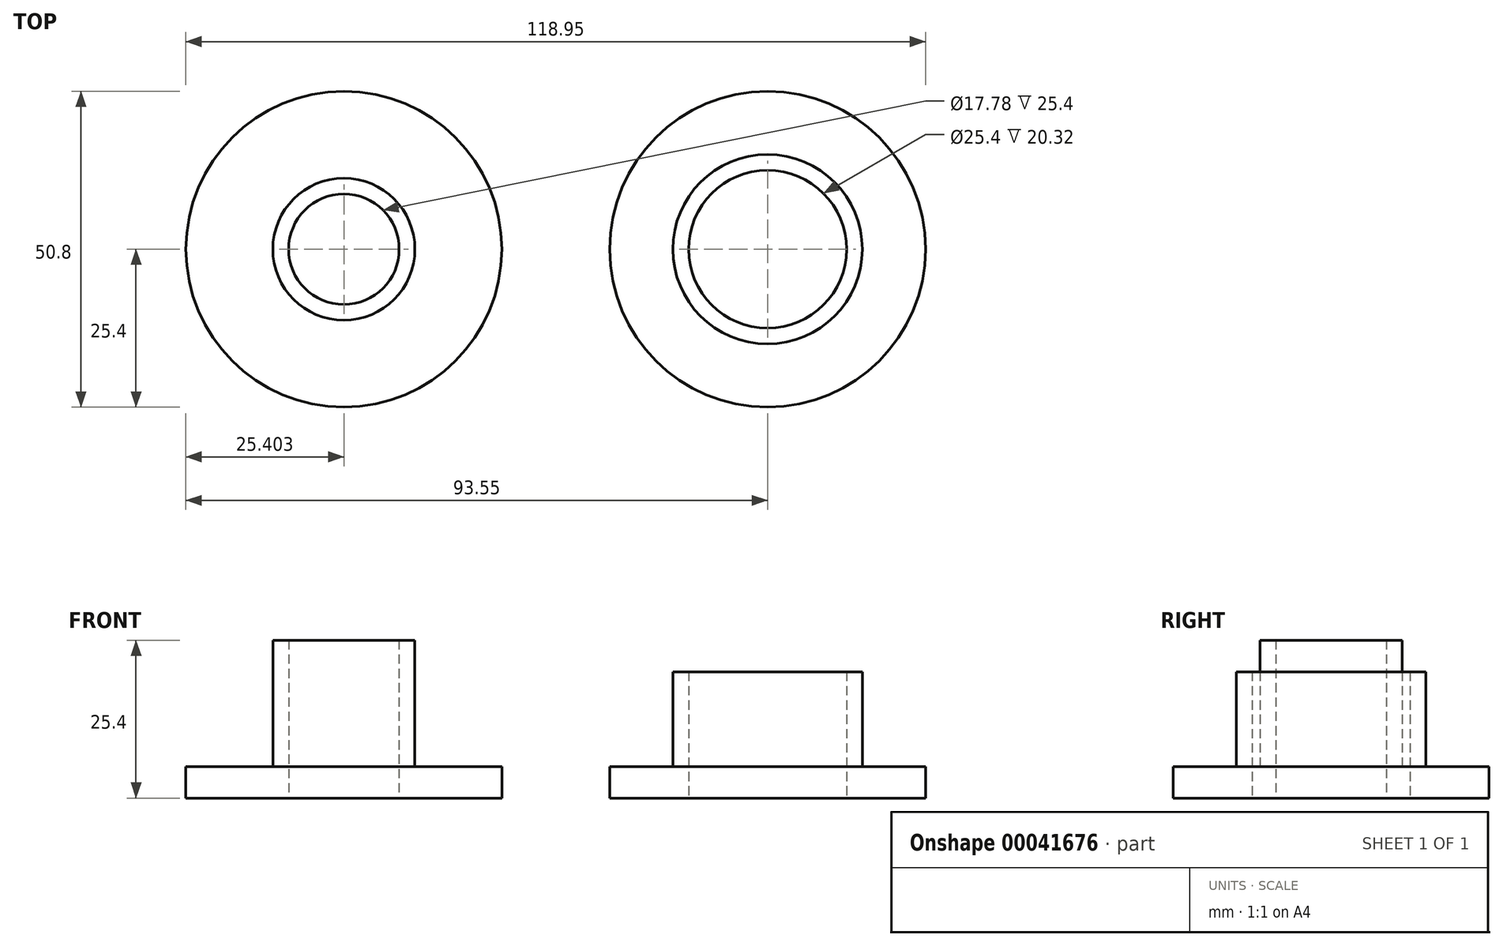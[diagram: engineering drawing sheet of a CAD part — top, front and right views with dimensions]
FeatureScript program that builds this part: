
annotation { "Feature Type Name" : "Feature", "Feature Type Description" : "" }
export const myFeature = defineFeature(function(context is Context, id is Id, definition is map)
    precondition{}
    {
        {
            var Q0;
            Q0=qCreatedBy(makeId("Top.planeOp"),FACE);
            var sketch = newSketch(context, id + "F0", { "sketchPlane" : qUnion([Q0])});
            skCircle(sketch, "E0", {"center": v(0, 0) * mm, "radius": 25.4 * mm});
            skCircle(sketch, "E1", {"center": v(0, 0) * mm, "radius": 12.7 * mm});
            skCircle(sketch, "E2.0", {"center": v(0, 0) * mm, "radius": 15.24 * mm});
            skSolve(sketch);
        }
        {
            var Q0;
            Q0 = qSketchRegion(id + "F0", true);
            extrude(context, id + "F1", {"entities" : qUnion([Q0]), "depth" : 5.08 * mm});
        }
        {
            var Q0;
            Q0=makeQuery(id+"F0.imprint","IMPRINT",FACE,{"disambiguationData":[TD([[makeQuery(id+"F0.imprint","IMPRINT",EDGE,{"derivedFrom":sQuery(id+"F0.wireOp",EDGE,"E1")}),-1.0]])]});
            extrude(context, id + "F2", {"entities" : qUnion([Q0]), "operationType" : NewBodyOperationType.ADD, "depth" : 20.32 * mm});
        }
        {
            var Q0;
            Q0=qCreatedBy(makeId("Top.planeOp"),FACE);
            var sketch = newSketch(context, id + "F3", { "sketchPlane" : qUnion([Q0])});
            skCircle(sketch, "E3", {"center": v(-68.15, 0) * mm, "radius": 25.4 * mm});
            skCircle(sketch, "E4", {"center": v(-68.15, 0) * mm, "radius": 11.43 * mm});
            skCircle(sketch, "E5.0", {"center": v(-68.15, 0) * mm, "radius": 8.9 * mm});
            skSolve(sketch);
        }
        {
            var Q0;
            Q0 = qSketchRegion(id + "F3", true);
            extrude(context, id + "F4", {"entities" : qUnion([Q0]), "depth" : 5.08 * mm});
        }
        {
            var Q0;
            Q0=makeQuery(id+"F3.imprint","IMPRINT",FACE,{"disambiguationData":[TD([[makeQuery(id+"F3.imprint","IMPRINT",EDGE,{"derivedFrom":sQuery(id+"F3.wireOp",EDGE,"E4")}),1.0]])]});
            extrude(context, id + "F5", {"entities" : qUnion([Q0]), "operationType" : NewBodyOperationType.ADD, "depth" : 25.4 * mm});
        }
    });
